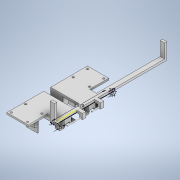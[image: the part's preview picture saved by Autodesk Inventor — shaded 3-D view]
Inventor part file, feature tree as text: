
AUTODESK INVENTOR PART (.ipt)
format: ipt  version: 2020.2 (Build 242310000, 310)  size: 762,880 bytes
history: native  units: mm
features: sketch x35, extrude x34, projected_geometry x12, hole x3
ambient origin geometry x8: Origin, YZ Plane, XZ Plane, XY Plane, X Axis, Y Axis, Z Axis, Center Point
bodies: Solid1 (feature_tree)
feature tree (84):
  sketch  "Sketch1"  dims[d0=8.0mm d1=98.298mm]
  extrude  "Extrusion1"  Depth=98.298mm
  extrude  "Extrusion2"  Depth=4.0mm
  extrude  "Extrusion3"  Depth=4.0mm TaperAngle=0.0deg
  extrude  "Extrusion4"  Depth=34.0mm
  extrude  "Extrusion5"  Depth=12.7mm
  extrude  "Extrusion6"  Depth=25.0mm
  hole  "Hole1"  [1 undecoded]
  extrude  "Extrusion11"  TaperAngle=60.0deg  [1 undecoded]
  extrude  "Extrusion12"  TaperAngle=120.0deg  [1 undecoded]
  sketch  "Sketch16"  dims[d19=6.4262mm d20=120.0deg]
  extrude  "Extrusion13"  Depth=6.4262mm
  extrude  "Extrusion14"  Depth=6.4262mm
  sketch  "Sketch17"  dims[d21=120.0deg d22=6.4262mm]
  extrude  "Extrusion15"  Depth=25.4mm TaperAngle=0.0deg
  extrude  "Extrusion18"  Depth=6.0mm
  extrude  "Extrusion19"  Depth=8.89mm
  extrude  "Extrusion20"  Depth=10.0mm
  hole  "Hole2"  [1 undecoded]
  extrude  "Extrusion21"  Depth=2.0mm
  extrude  "Extrusion22"  Depth=2.0mm
  sketch  "Sketch27"  dims[d45=8.89mm d46=2.0mm]
  extrude  "Extrusion23"  Depth=25.4mm
  extrude  "Extrusion24"  Depth=32.48mm
  extrude  "Extrusion25"  TaperAngle=90.0deg  [1 undecoded]
  sketch  "Sketch29"  dims[d79=51.53mm d80=32.48mm]
  extrude  "Extrusion26"  Depth=2.0mm
  extrude  "Extrusion27"  Depth=21.0mm
  extrude  "Extrusion28"  Depth=36.0mm TaperAngle=0.0deg
  sketch  "Sketch31"  dims[d83=4.0mm d84=0.0mm d87=2.0mm]
  extrude  "Extrusion29"  Depth=8.0mm
  extrude  "Extrusion30"  Depth=17.5mm
  extrude  "Extrusion32"  Depth=35.0mm
  extrude  "Extrusion33"  Depth=5.0mm
  extrude  "Extrusion34"  TaperAngle=90.0deg  [1 undecoded]
  extrude  "Extrusion35"  Depth=5.0mm
  extrude  "Extrusion37"  Depth=25.4mm TaperAngle=0.0deg
  extrude  "Extrusion38"  Depth=1.5mm
  extrude  "Extrusion39"  TaperAngle=0.0deg  [1 undecoded]
  extrude  "Extrusion40"  Depth=28.8036mm
  hole  "Hole4"  [1 undecoded]
  extrude  "Extrusion43"  Depth=6.4262mm
  extrude  "Extrusion44"  TaperAngle=120.0deg  [1 undecoded]
  sketch  "Sketch2"  dims[d2=8.0mm d3=4.0mm]
  sketch  "Sketch3"  dims[d4=4.0mm d5=4.0mm d6=0.0mm]
  sketch  "Sketch4"  dims[d7=34.0mm d8=0.0mm d9=19.558mm]
  sketch  "Sketch5"  dims[d10=16.1125mm d11=12.7mm]
  sketch  "Sketch6"  dims[d12=25.0mm d13=0.0mm d14=11.1125mm]
  sketch  "Sketch14"  dims[d15=6.4135mm d16=12.827mm]
  projected_geometry  "Projected Loop2"
  sketch  "Sketch15"  dims[d17=6.4262mm d18=60.0deg]
  projected_geometry  "Projected Loop3"
  sketch  "Sketch18"  dims[d23=120.0deg d24=6.4262mm]
  sketch  "Sketch21"  dims[d25=120.0deg d26=25.4mm d27=0.0mm]
  sketch  "Sketch22"  dims[d28=6.0mm d29=8.89mm]
  sketch  "Sketch23"  dims[d30=5.9944mm d31=8.89mm]
  sketch  "Sketch24"  dims[d32=25.4mm d33=0.0mm d34=10.0mm]
  sketch  "Sketch25"  dims[d35=90.0deg d36=20.0mm]
  projected_geometry  "Projected Loop5"
  sketch  "Sketch26"  dims[d37=3.4mm d38=19.05mm d39=6.2992mm d40=6.35mm d41=90.0deg d42=5.0mm d43=0.0mm d44=2.0mm]
  sketch  "Sketch28"  dims[d47=25.4mm d48=0.0mm d78=16.24mm]
  sketch  "Sketch30"  dims[d81=90.0deg d82=90.0deg]
  sketch  "Sketch32"  dims[d88=2.0mm d89=21.0mm]
  projected_geometry  "Projected Loop6"
  sketch  "Sketch33"  dims[d90=2.0mm d91=36.0mm d92=0.0mm]
  projected_geometry  "Projected Loop7"
  sketch  "Sketch35"  dims[d93=13.878mm d94=8.0mm]
  projected_geometry  "Projected Loop8"
  sketch  "Sketch36"  dims[d95=180.0deg d96=17.5mm]
  sketch  "Sketch37"  dims[d97=90.0deg d98=35.0mm]
  sketch  "Sketch38"  dims[d99=3.5mm d100=5.0mm]
  sketch  "Sketch41"  dims[d101=7.0mm d102=90.0deg]
  sketch  "Sketch42"  dims[d103=5.0mm d104=3.4mm]
  sketch  "Sketch43"  dims[d105=3.4mm d106=25.4mm d107=0.0mm]
  projected_geometry  "Projected Loop9"
  projected_geometry  "Projected Loop10"
  projected_geometry  "Projected Loop11"
  projected_geometry  "Projected Loop12"
  sketch  "Sketch44"  dims[d108=6.4262mm d109=0.0mm d110=1.5mm]
  sketch  "Sketch45"  dims[d111=1.5mm d112=0.0mm d113=0.0mm]
  sketch  "Sketch48"  dims[d128=44.8mm d129=28.8036mm]
  sketch  "Sketch49"  dims[d130=25.4mm d131=0.0mm d132=3.2131mm d133=6.4262mm d134=120.0deg d135=3.2131mm d136=6.4262mm d137=120.0deg d138=25.4mm d139=0.0mm d140=8.001mm d141=13.8938mm d142=8.001mm d143=0.0mm d144=25.4mm d145=0.0mm d146=10.0mm d147=20.0mm d148=3.4mm d149=19.05mm d150=6.2992mm d151=6.35mm d152=90.0deg d153=5.0mm d154=0.0mm d155=16.2433mm d156=32.4866mm d157=51.5366mm d158=4.0mm d159=0.0mm d160=21.0mm d161=2.0mm d162=2.0mm d163=2.0mm d164=2.0mm d165=36.0mm d166=0.0mm d167=7.0mm d168=5.0mm d169=5.0mm d170=17.5mm d171=35.0mm d172=3.4mm d173=3.4mm d174=5.0mm d175=0.0mm d176=5.0mm d177=0.0mm d178=1.5mm d179=1.5mm d180=25.4mm d181=0.0mm d182=19.05mm d183=10.0mm d184=5.08mm d185=4.0mm d186=0.0mm d187=10.0mm d188=0.0mm d189=2.0mm d190=2.0mm d191=25.4mm d192=0.0mm d193=10.0mm d194=30.0mm d195=0.0mm d196=99.06mm d197=0.0mm d201=11.43mm d202=0.0mm d203=25.4mm d204=0.0mm d205=25.4mm d206=0.0mm d207=25.4mm d208=0.0mm d237=25.4mm d238=0.0mm d239=25.4mm d240=0.0mm d241=1.5mm d242=0.0mm d243=39.0mm d244=35.0mm d245=39.0mm d246=35.0mm d247=3.0mm d248=0.0mm d249=5.0mm d250=5.0mm d251=29.7mm d252=26.05mm d253=4.0mm d254=4.0mm d255=29.7mm d256=26.05mm d257=3.4mm d258=19.05mm d259=6.2992mm d260=6.35mm d261=90.0deg d262=25.4mm d263=20.594885mm d271=4.0mm d272=25.4mm d273=0.0mm d274=25.4mm d275=0.0mm d214=12.7mm d215=0.872665mm d216=12.7mm d217=0.872665mm d228=12.7mm d229=0.872665mm d230=12.7mm d231=0.872665mm]
  projected_geometry  "Projected Loop13"
  projected_geometry  "Projected Loop14"
note: 9 required parameter values undecoded (feature->parameter linkage not recoverable at this tier; creation-order binding heuristic only, values carry confidence <= 0.55)
